# Revit family: Toilet-Floor_Mount-KOHLER-SAN_RAPHAEL-K-8688T
name_source: partatom
category: Plumbing Fixtures
units: mm (PartAtom-declared; Revit-internal decimal feet)

## family parameters
Cut with Voids When Loaded = No
Host = Face
OmniClass Number = 23.31.19.00
OmniClass Title = Toilets
Part Type = Normal
Room Calculation Point = No
Round Connector Dimension = Use Diameter
Shared = No

## types (2) — shared parameters
ADA Compliant = No
Assembly Code = D2010100
CW Connection = Yes
Cold Water Inlet = Cold Water Inlet
Date Modified = 6/20/2024
Default Elevation = 0"
Finish = Kohler-Vitreous_China-0-White
Flow Rate = 0 GPM
Flush Rate- GPF = 0 GPF
Flush Rate- LPF = 4.8 LPF
HW Connection = No
Height = 24 9/16"
Hot Water Inlet = Hot Water Inlet
Length = 29"
Manufacturer = Kohler Co.
Master Format 2014 = 22 42 13.13
Master Format 2014 Name = Residential Water Closets
Material = Vitreous China
Pressure = 0.00 psi
Product Name = SAN RAPHAEL
Rough-In = 12"
Seat Included = Yes
URL = http://www.kohler.com.cn
Vent Connection = No
Waste Connection = Yes
Waste Water Outlet = Waste Water Outlet
WaterSense Certified = No
Width = 20 1/2"

## per-type parameters (varying)
| type | Description | Model | Product Documentation Link | Product Page URL | Type |
| S, 0-White | GRANDE SKIRTED 1 PC TLT 305 | K-8688T-S-0 | https://files.kohler.com.cn | https://www.kohler.com.cn | 1 |
| TPF, 0-White | GRANDE TOUCHLESS 1 PC TLT | K-8688T-TPF-0 |  |  | 2 |

## geometry (parser evidence)
native form markers: Sweep x5
no freeform markers — native parametric forms only
